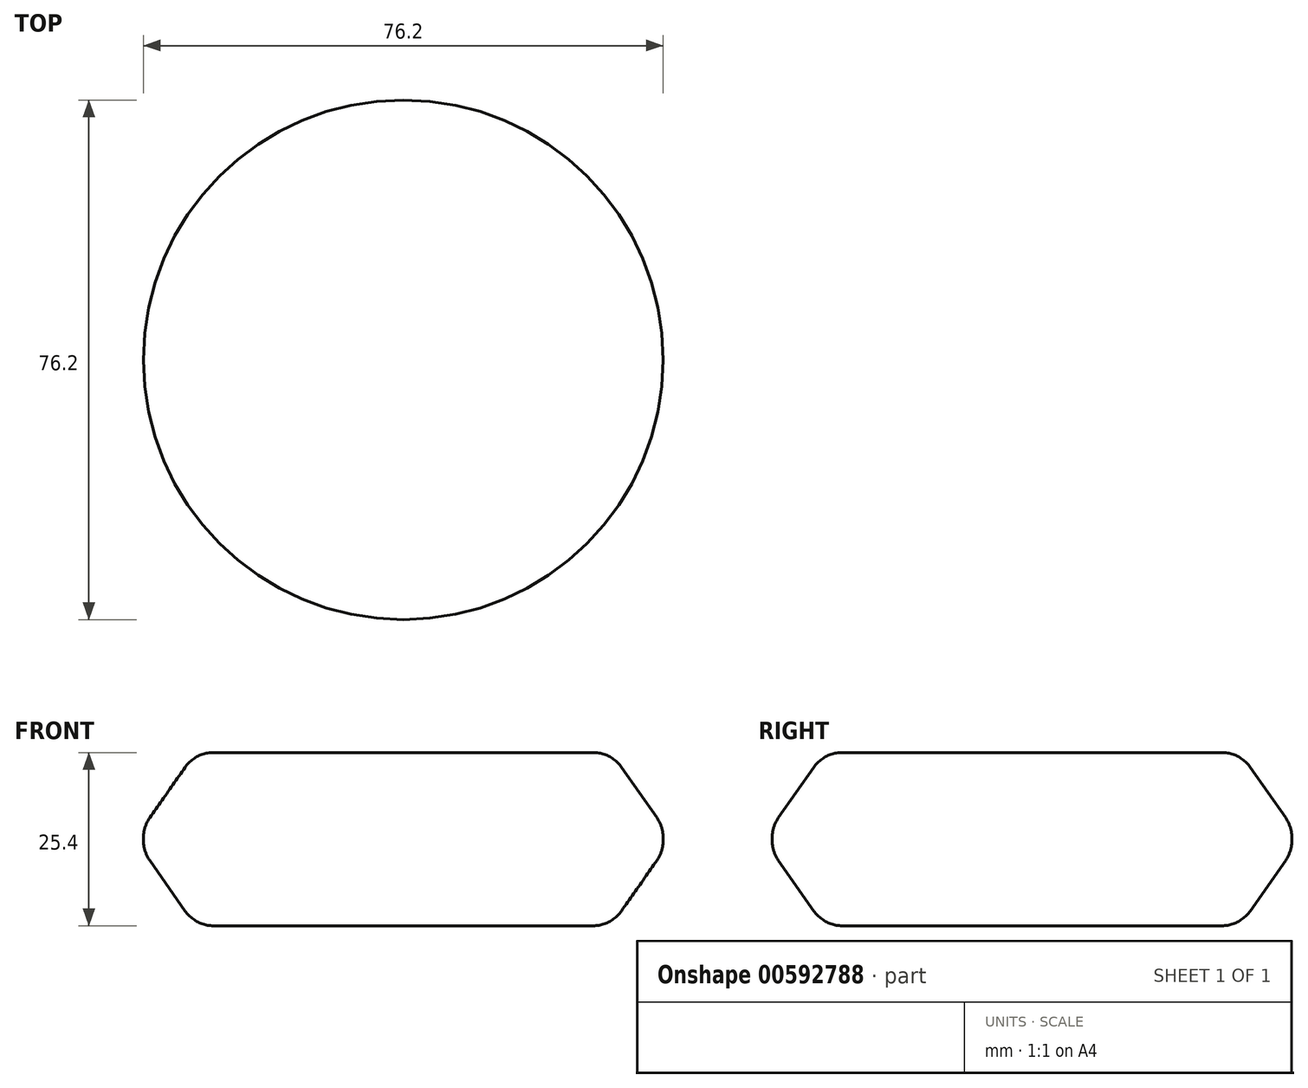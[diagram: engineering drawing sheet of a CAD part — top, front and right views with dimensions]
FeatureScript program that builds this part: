
annotation { "Feature Type Name" : "Feature", "Feature Type Description" : "" }
export const myFeature = defineFeature(function(context is Context, id is Id, definition is map)
    precondition{}
    {
        {
            var Q0;
            Q0=qCreatedBy(makeId("Top.planeOp"),FACE);
            var sketch = newSketch(context, id + "F0", { "sketchPlane" : qUnion([Q0])});
            skCircle(sketch, "E0", {"center": v(0, 0) * mm, "radius": 38.1 * mm});
            skSolve(sketch);
        }
        {
            var Q0;
            Q0=makeQuery(id+"F0.imprint","IMPRINT",FACE,{"disambiguationData":[TD([[makeQuery(id+"F0.imprint","IMPRINT",EDGE,{"derivedFrom":sQuery(id+"F0.wireOp",EDGE,"E0")}),1.0]])]});
            extrude(context, id + "F1", {"entities" : qUnion([Q0]), "endBound" : BoundingType.SYMMETRIC, "depth" : 25.4 * mm, "offsetDistance" : 25.4 * mm});
        }
        {
            var Q0;
            Q0=makeQuery(id+"F1.opExtrude","CAP_EDGE",EDGE,{"disambiguationData":[OSD([sQuery(id+"F0.wireOp",EDGE,"E0")])],"isStart":false});
            var Q1;
            Q1=makeQuery(id+"F1.opExtrude","CAP_EDGE",EDGE,{"disambiguationData":[OSD([sQuery(id+"F0.wireOp",EDGE,"E0")])],"isStart":true});
            chamfer(context, id + "F2", {"entities" : qUnion([Q0, Q1]), "chamferType" : ChamferType.OFFSET_ANGLE, "width" : 7.62 * mm, "oppositeDirection" : false, "angle" : 55 * degree, "tangentPropagation" : true});
        }
        {
            var Q0;
            {var subQ0=sQuery(id+"F0.wireOp",EDGE,"E0");Q0=makeQuery(id+"F2.opChamfer","BLEND_EDGE",EDGE,{"blendedFrom":[makeQuery(id+"F1.opExtrude","CAP_EDGE",EDGE,{"disambiguationData":[OSD([subQ0])],"isStart":false}),makeQuery(id+"F1.opExtrude","SWEPT_FACE",FACE,{"disambiguationData":[OSD([subQ0])]})],"blendedInto":[makeQuery(id+"F1.opExtrude","SWEPT_FACE",FACE,{"disambiguationData":[OSD([subQ0])]})]});}
            var Q1;
            Q1=makeQuery(id+"F1.opExtrude","CAP_FACE",FACE,{"disambiguationData":[OSD([sQuery(id+"F0.wireOp",EDGE,"E0")])],"isStart":false});
            var Q2;
            {var subQ0=sQuery(id+"F0.wireOp",EDGE,"E0");Q2=makeQuery(id+"F2.opChamfer","BLEND_EDGE",EDGE,{"blendedFrom":[makeQuery(id+"F1.opExtrude","CAP_EDGE",EDGE,{"disambiguationData":[OSD([subQ0])],"isStart":true}),makeQuery(id+"F1.opExtrude","SWEPT_FACE",FACE,{"disambiguationData":[OSD([subQ0])]})],"blendedInto":[makeQuery(id+"F1.opExtrude","SWEPT_FACE",FACE,{"disambiguationData":[OSD([subQ0])]})]});}
            var Q3;
            {var subQ0=sQuery(id+"F0.wireOp",EDGE,"E0");Q3=makeQuery(id+"F2.opChamfer","BLEND_EDGE",EDGE,{"blendedFrom":[makeQuery(id+"F1.opExtrude","CAP_EDGE",EDGE,{"disambiguationData":[OSD([subQ0])],"isStart":true}),makeQuery(id+"F1.opExtrude","CAP_FACE",FACE,{"disambiguationData":[OSD([subQ0])],"isStart":true})],"blendedInto":[makeQuery(id+"F1.opExtrude","CAP_FACE",FACE,{"disambiguationData":[OSD([subQ0])],"isStart":true})]});}
            fillet(context, id + "F3", {"entities" : qUnion([Q0, Q1, Q2, Q3]), "radius" : 5.08 * mm, "tangentPropagation" : true, "allowEdgeOverflow" : false});
        }
    });
